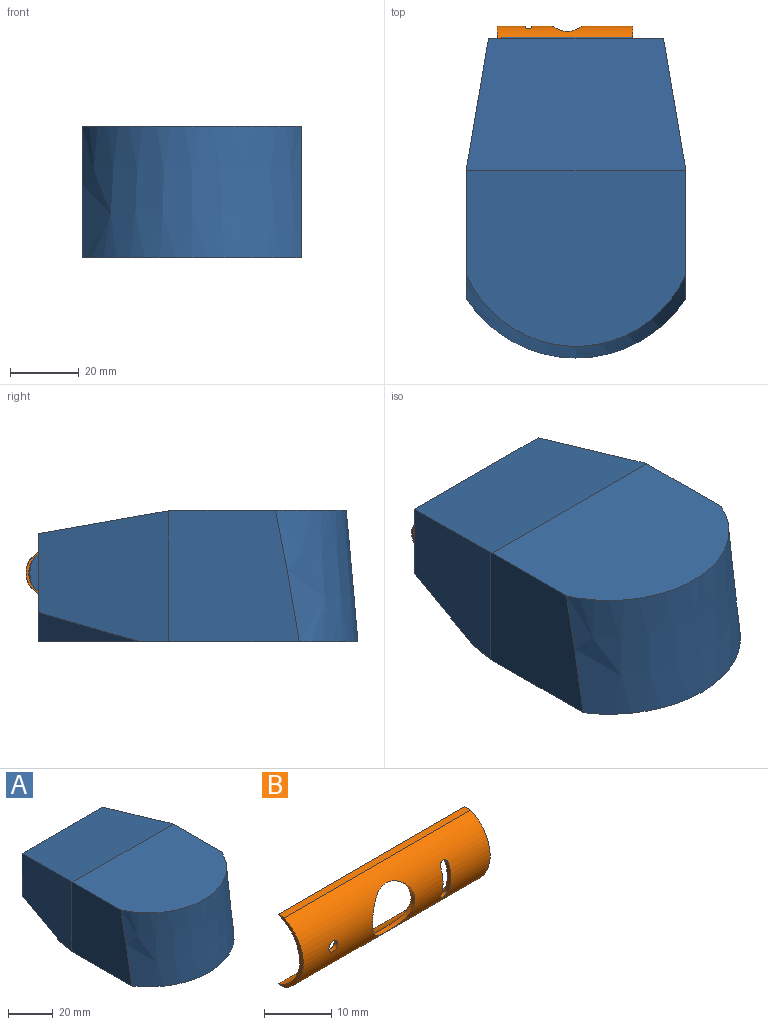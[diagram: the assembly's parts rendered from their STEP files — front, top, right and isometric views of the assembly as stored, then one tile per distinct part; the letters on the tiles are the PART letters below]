
ASSEMBLY  parts=2 mates=1
PART A: 27 faces, bbox 69.6x95.2x38.1 mm
  f0: plane 38.1x38.1mm, normal (-1,0,0), area 1326.8mm2, adj f4,f5,f6,f7,f8,f11
  f1: plane 38.1x38.1mm, normal (1,0,0), area 1326.8mm2, adj f2,f5,f6,f7,f8,f9
  f2: plane 37.94x37.57mm, normal (0.99,0.17,0), area 1194mm2, adj f1,f3,f8,f9,f12
  f3: plane 50.8x31.31mm, normal (0,1,0), area 1004.5mm2, adj f2,f4,f8,f10,f12,f13,f17,f18
  f4: plane 37.94x37.57mm, normal (-0.99,0.17,0), area 1194mm2, adj f0,f3,f8,f11,f13
  f5: plane 63.5x51.02mm, normal (0,0,1), area 2873.2mm2, adj f0,f1,f7,f8
  f6: plane 92.68x63.5mm, normal (0,0,-1), area 4971.7mm2, adj f0,f1,f7,f9,f10,f11,f12,f13
  f7: cone r=38.1mm half-angle=5deg, axis (0,0,-1), area 2954.5mm2, adj f0,f1,f5,f6
  f8: plane 63.5x38.35mm, normal (0,0.17,0.98), area 2230.8mm2, adj f0,f1,f2,f3,f4,f5
  f9: plane 8.54x1.44mm, normal (0.7,0.12,-0.71), area 0.3mm2, adj f1,f2,f6,f12
  f10: plane 26.62x0.03mm, normal (0,0.71,-0.71), area 1mm2, adj f3,f6,f12,f13
  f11: plane 8.54x1.44mm, normal (-0.7,0.12,-0.71), area 0.3mm2, adj f0,f4,f6,f13
  f12: plane 29.2x17.04mm, normal (0.54,0.32,-0.78), area 228.3mm2, adj f2,f3,f6,f9,f10
  f13: plane 29.2x17.04mm, normal (-0.54,0.32,-0.78), area 228.3mm2, adj f3,f4,f6,f10,f11
  f14: plane 5.08x2.54mm, normal (1,0,0), area 12.3mm2, adj f15,f21,f24,f25,f26
  f15: cylinder r=0.83mm len=2.18mm, axis (0,-1,0), area 5.2mm2, adj f14,f16,f24,f26
  f16: plane 5.08x2.54mm, normal (-1,0,0), area 12.3mm2, adj f15,f21,f24,f25,f26
  f17: plane 12.7x2.54mm, normal (1,0,0), area 22.1mm2, adj f3,f25,f26
  f18: plane 12.7x2.54mm, normal (-1,0,0), area 22.1mm2, adj f3,f25,f26
  f19: cylinder r=4.45mm len=8.89mm, axis (0,-1,0), area 55.1mm2, adj f22,f25,f26
  f20: cylinder r=0.95mm len=2.54mm, axis (0,-1,0), area 15mm2, adj f23,f25,f26
  f21: cylinder r=0.83mm len=2.18mm, axis (0,-1,0), area 5.2mm2, adj f14,f16,f24,f25
  f22: plane 8.89x8.89mm, normal (0,1,0), area 62.1mm2, adj f19
  f23: plane 1.91x1.91mm, normal (0,1,0), area 2.9mm2, adj f20
  f24: plane 6.73x1.65mm, normal (0,1,0), area 10.5mm2, adj f14,f15,f16,f21
  f25: cylinder r=9.27mm len=38.1mm, axis (-1,0,0), area 228mm2, adj f3,f14,f16,f17,f18,f19,f20,f21
  f26: cylinder r=9.27mm len=38.1mm, axis (1,0,0), area 228mm2, adj f3,f14,f15,f16,f17,f18,f19,f20
PART B: 12 faces, bbox 39.4x5.3x12.7 mm
  f0: cylinder r=6.7mm len=39.37mm, axis (-1,0,0), area 577.9mm2, adj f2,f3,f4,f5,f6,f7,f8,f9
  f1: cylinder r=6.99mm len=39.37mm, axis (-1,0,0), area 547.4mm2, adj f2,f3,f4,f5,f6,f7,f8,f9
  f2: plane 39.37x1.27mm, normal (0,0,1), area 50mm2, adj f0,f1,f4,f5
  f3: plane 39.37x1.27mm, normal (0,0,-1), area 50mm2, adj f0,f1,f4,f5
  f4: plane 12.7x5.33mm, normal (1,0,0), area 10.7mm2, adj f0,f1,f2,f3
  f5: plane 12.7x5.33mm, normal (-1,0,0), area 10.7mm2, adj f0,f1,f2,f3
  f6: cylinder r=4.45mm len=8.89mm, axis (0,1,0), area 22.4mm2, adj f0,f1
  f7: cylinder r=0.95mm len=1.91mm, axis (0,1,0), area 4.6mm2, adj f0,f1
  f8: plane 5.08x1.26mm, normal (-1,0,0), area 3.9mm2, adj f0,f1,f9,f11
  f9: cylinder r=0.83mm len=1.65mm, axis (0,1,0), area 2.1mm2, adj f0,f1,f8,f10
  f10: plane 5.08x1.26mm, normal (1,0,0), area 3.9mm2, adj f0,f1,f9,f11
  f11: cylinder r=0.83mm len=1.65mm, axis (0,1,0), area 2.1mm2, adj f0,f1,f8,f10
PLACE A t=(9.74,-22.3,12.47)mm
PLACE B rot(axis=(0,0,-1),180deg) t=(-5.51,51.69,26.04)mm
MATE fastened B.f0 <-> A.f17  axis (1,0,0) through (-5.51,49.56,32.39)mm
